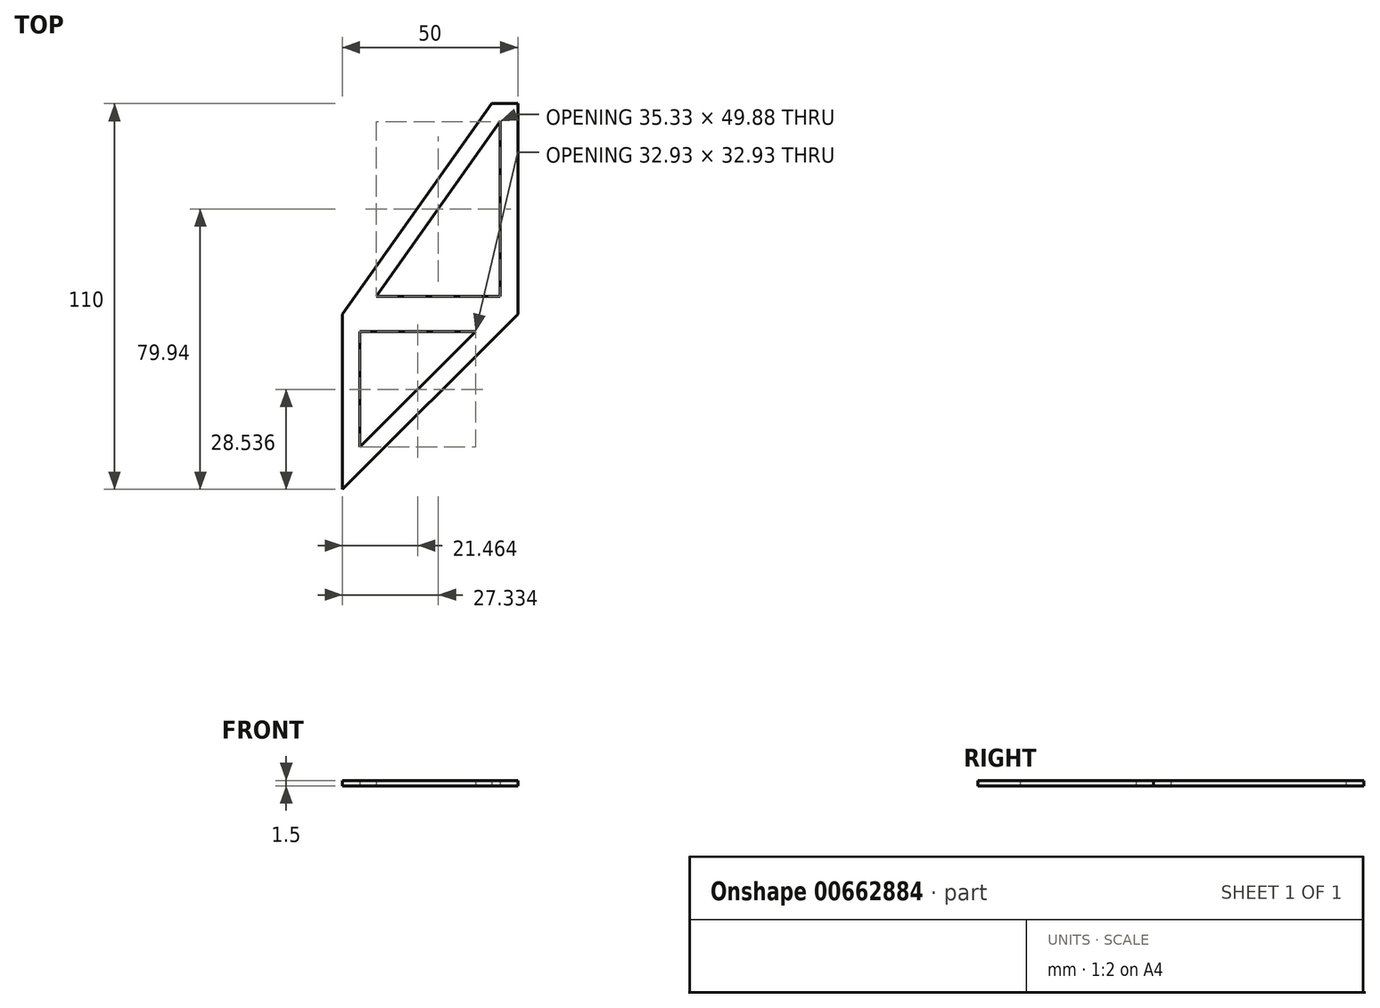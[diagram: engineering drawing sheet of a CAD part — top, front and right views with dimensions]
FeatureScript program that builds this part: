
annotation { "Feature Type Name" : "Feature", "Feature Type Description" : "" }
export const myFeature = defineFeature(function(context is Context, id is Id, definition is map)
    precondition{}
    {
        {
            var Q0;
            Q0=qCreatedBy(makeId("Top.planeOp"),FACE);
            var sketch = newSketch(context, id + "F0", { "sketchPlane" : qUnion([Q0])});
            skLineSegment(sketch, "E0", {"start": v(0, 0) * mm, "end": v(50, 0) * mm});
            skLineSegment(sketch, "E1", {"start": v(50, 0) * mm, "end": v(50, 60) * mm});
            skLineSegment(sketch, "E2", {"start": v(50, 60) * mm, "end": v(42.5, 60) * mm});
            skLineSegment(sketch, "E3", {"start": v(42.5, 60) * mm, "end": v(0, 0) * mm});
            skLineSegment(sketch, "E4", {"start": v(0, -50) * mm, "end": v(50, 0) * mm});
            skLineSegment(sketch, "E5", {"start": v(0, 0) * mm, "end": v(0, -50) * mm});
            skLineSegment(sketch, "E6.0", {"start": v(45, 54.88) * mm, "end": v(9.67, 5) * mm});
            skLineSegment(sketch, "E6.1", {"start": v(45, 5) * mm, "end": v(45, 54.88) * mm});
            skLineSegment(sketch, "E6.2", {"start": v(9.67, 5) * mm, "end": v(45, 5) * mm});
            skLineSegment(sketch, "E7.0", {"start": v(5, -5) * mm, "end": v(5, -37.93) * mm});
            skLineSegment(sketch, "E7.1", {"start": v(5, -5) * mm, "end": v(37.93, -5) * mm});
            skLineSegment(sketch, "E7.2", {"start": v(5, -37.93) * mm, "end": v(37.93, -5) * mm});
            skSolve(sketch);
        }
        {
            var Q0;
            Q0 = qSketchRegion(id + "F0", true);
            extrude(context, id + "F1", {"entities" : qUnion([Q0]), "depth" : 1.5 * mm, "offsetDistance" : 25 * mm});
        }
    });
